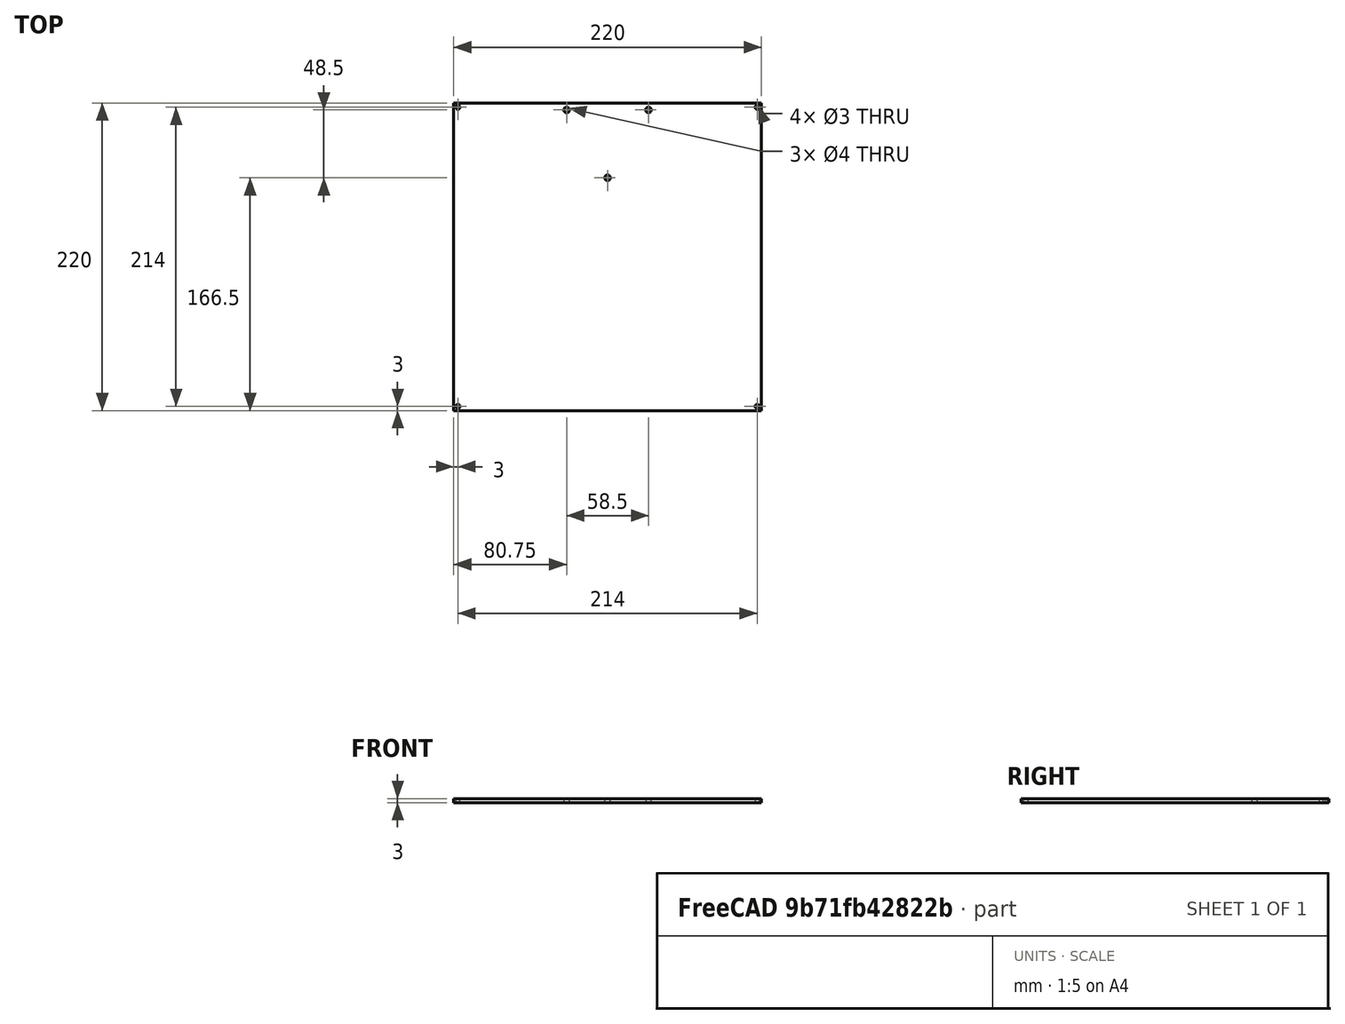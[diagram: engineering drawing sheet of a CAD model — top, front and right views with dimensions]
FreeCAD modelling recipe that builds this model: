
FCSTD DOCUMENT  (FreeCAD 0.16R6712 (Git))
Label: build-plate
License: All rights reserved
LicenseURL: http://en.wikipedia.org/wiki/All_rights_reserved
objects: Sketcher::SketchObject×1, PartDesign::Pad×1
note: 3 computed .brp shape members not serialized (recipe doc carries the construction recipe); baked Part::Feature solids carry a one-line shape summary decoded from their .brp

FEATURE [Sketcher::SketchObject] Sketch
  sketch-geometry (11):
    g0: LineSegment StartX=-110 StartY=110 StartZ=0 EndX=110 EndY=110 EndZ=0
    g1: LineSegment StartX=110 StartY=110 StartZ=0 EndX=110 EndY=-110 EndZ=0
    g2: LineSegment StartX=110 StartY=-110 StartZ=0 EndX=-110 EndY=-110 EndZ=0
    g3: LineSegment StartX=-110 StartY=-110 StartZ=0 EndX=-110 EndY=110 EndZ=0
    g4: Circle CenterX=-107 CenterY=107 CenterZ=0 NormalX=0 NormalY=0 NormalZ=1 Radius=1.5
    g5: Circle CenterX=107 CenterY=107 CenterZ=0 NormalX=0 NormalY=0 NormalZ=1 Radius=1.5
    g6: Circle CenterX=107 CenterY=-107 CenterZ=0 NormalX=0 NormalY=0 NormalZ=1 Radius=1.5
    g7: Circle CenterX=-107 CenterY=-107 CenterZ=0 NormalX=0 NormalY=0 NormalZ=1 Radius=1.5
    g8: Circle CenterX=-29.25 CenterY=105 CenterZ=0 NormalX=0 NormalY=0 NormalZ=1 Radius=2
    g9: Circle CenterX=29.25 CenterY=105 CenterZ=0 NormalX=0 NormalY=0 NormalZ=1 Radius=2
    g10: Circle CenterX=0 CenterY=56.5 CenterZ=0 NormalX=0 NormalY=0 NormalZ=1 Radius=2
  constraints (29):
    c: Coincident(g0,g1)
    c: Coincident(g1,g2)
    c: Coincident(g2,g3)
    c: Coincident(g3,g0)
    c: Horizontal(g0)
    c: Horizontal(g2)
    c: Vertical(g1)
    c: Vertical(g3)
    c: Equal(g0,g1)
    c: DistanceX(g0,g0) = 220
    c: DistanceX(g-1,g0) = 110
    c: DistanceY(g-1,g0) = 110
    c: Symmetric(g7,g4,g-1)
    c: Symmetric(g5,g4,g-2)
    c: Symmetric(g6,g7,g-2)
    c: Equal(g4,g5)
    c: Equal(g5,g6)
    c: Equal(g6,g7)
    c: Radius(g4) = 1.5
    c: DistanceX(g7,g6) = 214
    c: DistanceY(g7,g4) = 214
    c: Symmetric(g8,g9,g-2)
    c: PointOnObject(g10,g-2)
    c: DistanceY(g10,g9) = 48.5
    c: DistanceX(g8,g9) = 58.5
    c: Equal(g8,g10)
    c: Equal(g10,g9)
    c: Radius(g8) = 2
    c: DistanceY(g8,g0) = 5
FEATURE [PartDesign::Pad] Pad
  Length = 3
  Length2 = 100
  Sketch = -> Sketch
  Type = 0
